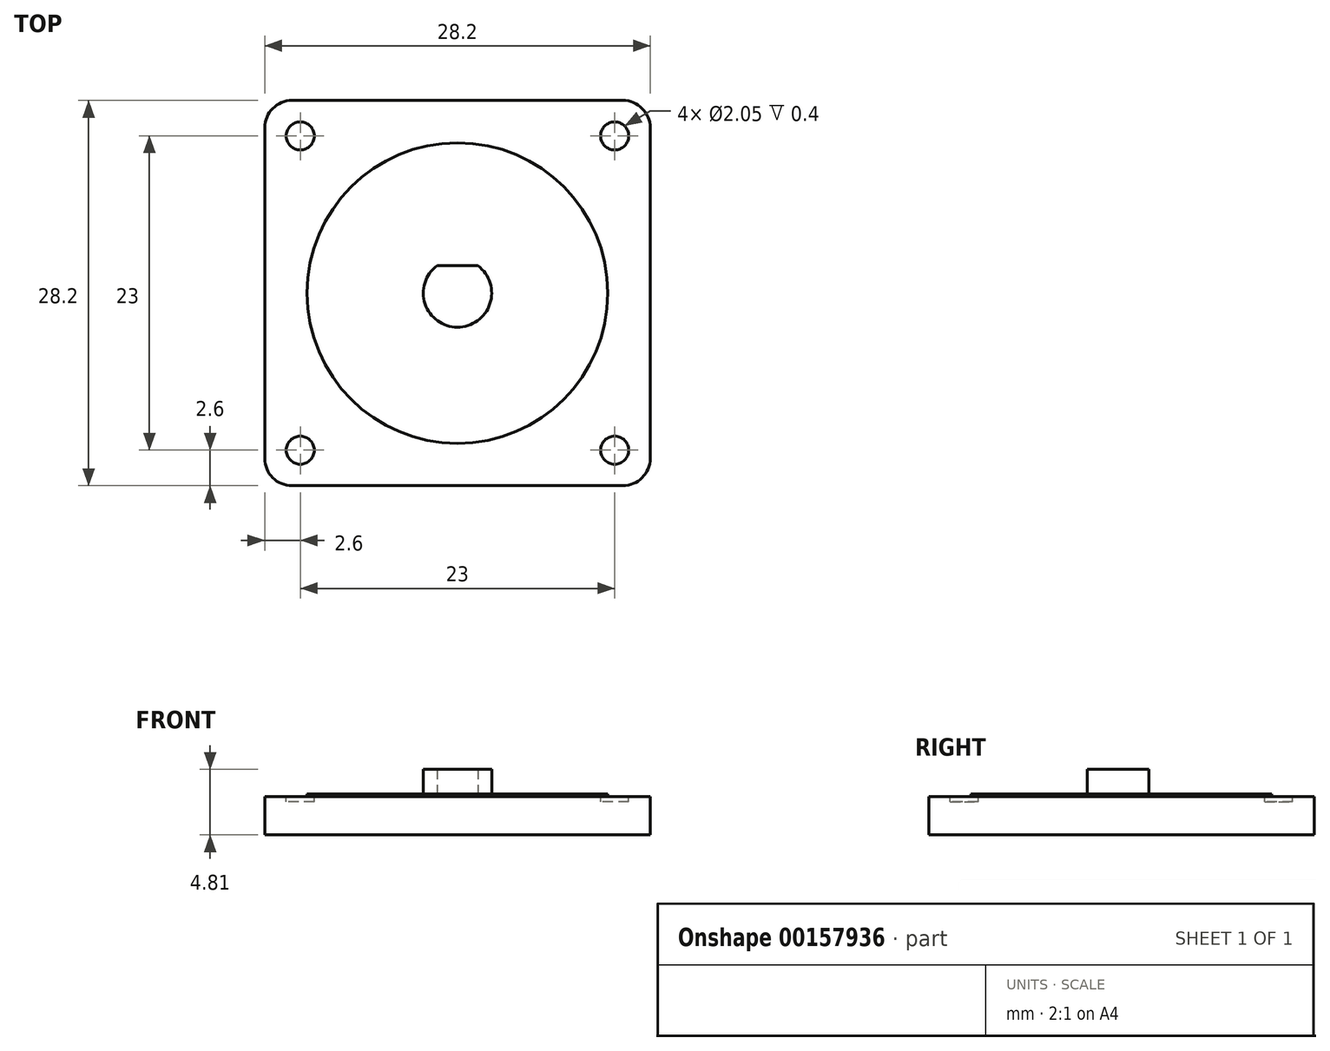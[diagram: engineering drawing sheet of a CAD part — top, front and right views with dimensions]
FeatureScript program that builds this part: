
annotation { "Feature Type Name" : "Feature", "Feature Type Description" : "" }
export const myFeature = defineFeature(function(context is Context, id is Id, definition is map)
    precondition{}
    {
        {
            assignVariable(context, id + "F0", {"name" : "h", "anyValue" : 2.81});
        }
        {
            assignVariable(context, id + "F1", {"name" : "Sd", "anyValue" : 0.4});
        }
        {
            assignVariable(context, id + "F2", {"name" : "Rh", "anyValue" : 0.2});
        }
        {
            assignVariable(context, id + "F3", {"name" : "Pl", "anyValue" : 2});
        }
        {
            var Q0;
            Q0=qCreatedBy(makeId("Top.planeOp"),FACE);
            var sketch = newSketch(context, id + "F4", { "sketchPlane" : qUnion([Q0])});
            skLineSegment(sketch, "E0.bottom", {"start": v(12.1, 14.1) * mm, "end": v(-12.1, 14.1) * mm});
            skLineSegment(sketch, "E0.top", {"start": v(12.1, -14.1) * mm, "end": v(-12.1, -14.1) * mm});
            skLineSegment(sketch, "E0.left", {"start": v(14.1, 12.1) * mm, "end": v(14.1, -12.1) * mm});
            skLineSegment(sketch, "E0.right", {"start": v(-14.1, 12.1) * mm, "end": v(-14.1, -12.1) * mm});
            skPoint(sketch, "E0.middle", {"position": v(0, 0) * mm});
            skCircle(sketch, "E1", {"center": v(0, 0) * mm, "radius": 11 * mm});
            skPoint(sketch, "E2.visualSharp", {"position": v(14.1, 14.1) * mm});
            skArc(sketch, "E2.filletArc", {"start": v(14.1, 12.1) * mm, "mid": v(13.51, 13.51) * mm, "end": v(12.1, 14.1) * mm});
            skPoint(sketch, "E3.visualSharp", {"position": v(14.1, -14.1) * mm});
            skArc(sketch, "E3.filletArc", {"start": v(12.1, -14.1) * mm, "mid": v(13.51, -13.51) * mm, "end": v(14.1, -12.1) * mm});
            skPoint(sketch, "E4.visualSharp", {"position": v(-14.1, -14.1) * mm});
            skArc(sketch, "E4.filletArc", {"start": v(-14.1, -12.1) * mm, "mid": v(-13.51, -13.51) * mm, "end": v(-12.1, -14.1) * mm});
            skPoint(sketch, "E5.visualSharp", {"position": v(-14.1, 14.1) * mm});
            skArc(sketch, "E5.filletArc", {"start": v(-12.1, 14.1) * mm, "mid": v(-13.51, 13.51) * mm, "end": v(-14.1, 12.1) * mm});
            skCircle(sketch, "E6", {"center": v(11.5, 11.5) * mm, "radius": 1.02 * mm});
            skCircle(sketch, "E7.MirrorC", {"center": v(-11.5, 11.5) * mm, "radius": 1.02 * mm});
            skCircle(sketch, "E8.MirrorC", {"center": v(11.5, -11.5) * mm, "radius": 1.02 * mm});
            skCircle(sketch, "E9.MirrorC", {"center": v(-11.5, -11.5) * mm, "radius": 1.02 * mm});
            skCircle(sketch, "E10", {"center": v(0, 0) * mm, "radius": 2.5 * mm});
            skLineSegment(sketch, "E11", {"start": v(-1.5, 2) * mm, "end": v(1.5, 2) * mm});
            skSolve(sketch);
        }
        {
            var Q0;
            Q0=makeQuery(id+"F4.imprint","IMPRINT",FACE,{"disambiguationData":[TD([[makeQuery(id+"F4.imprint","IMPRINT",EDGE,{"derivedFrom":sQuery(id+"F4.wireOp",EDGE,"E0.bottom")}),1.0]])]});
            var sketch = newSketch(context, id + "F5", { "sketchPlane" : qUnion([Q0])});
            skArc(sketch, "E12.0", {"start": v(-12.1, 14.1) * mm, "mid": v(-13.51, 13.51) * mm, "end": v(-14.1, 12.1) * mm});
            skLineSegment(sketch, "E12.1", {"start": v(12.1, 14.1) * mm, "end": v(-12.1, 14.1) * mm});
            skArc(sketch, "E12.2", {"start": v(14.1, 12.1) * mm, "mid": v(13.51, 13.51) * mm, "end": v(12.1, 14.1) * mm});
            skLineSegment(sketch, "E12.3", {"start": v(14.1, 12.1) * mm, "end": v(14.1, -12.1) * mm});
            skArc(sketch, "E12.4", {"start": v(12.1, -14.1) * mm, "mid": v(13.51, -13.51) * mm, "end": v(14.1, -12.1) * mm});
            skLineSegment(sketch, "E12.5", {"start": v(12.1, -14.1) * mm, "end": v(-12.1, -14.1) * mm});
            skArc(sketch, "E12.6", {"start": v(-14.1, -12.1) * mm, "mid": v(-13.51, -13.51) * mm, "end": v(-12.1, -14.1) * mm});
            skLineSegment(sketch, "E12.7", {"start": v(-14.1, 12.1) * mm, "end": v(-14.1, -12.1) * mm});
            skSolve(sketch);
        }
        {
            var Q0;
            Q0 = qSketchRegion(id + "F5", true);
            extrude(context, id + "F6", {"entities" : qUnion([Q0]), "depth" : (getVariable(context, 'h')) * mm});
        }
        {
            var Q0;
            Q0=makeQuery(id+"F6.opExtrude","CAP_FACE",FACE,{"disambiguationData":[OSD([sQuery(id+"F5.wireOp",EDGE,"E12.0"),sQuery(id+"F5.wireOp",EDGE,"E12.1"),sQuery(id+"F5.wireOp",EDGE,"E12.2"),sQuery(id+"F5.wireOp",EDGE,"E12.3"),sQuery(id+"F5.wireOp",EDGE,"E12.4"),sQuery(id+"F5.wireOp",EDGE,"E12.5"),sQuery(id+"F5.wireOp",EDGE,"E12.6"),sQuery(id+"F5.wireOp",EDGE,"E12.7")])],"isStart":false});
            var sketch = newSketch(context, id + "F7", { "sketchPlane" : qUnion([Q0])});
            skCircle(sketch, "E13.0", {"center": v(0, 0) * mm, "radius": 11 * mm});
            skSolve(sketch);
        }
        {
            var Q0;
            Q0=makeQuery(id+"F7.imprint","IMPRINT",FACE,{"disambiguationData":[TD([[makeQuery(id+"F7.imprint","IMPRINT",EDGE,{"derivedFrom":sQuery(id+"F7.wireOp",EDGE,"E13.0")}),-1.0]])]});
            var sketch = newSketch(context, id + "F8", { "sketchPlane" : qUnion([Q0])});
            skCircle(sketch, "E14.0", {"center": v(0, 0) * mm, "radius": 2.5 * mm});
            skLineSegment(sketch, "E14.1", {"start": v(-1.5, 2) * mm, "end": v(1.5, 2) * mm});
            skSolve(sketch);
        }
        {
            var Q0;
            Q0 = qSketchRegion(id + "F7", true);
            var Q1;
            Q1=sQuery(id+"F4.wireOp",EDGE,"E1");
            var Q2;
            Q2 = qConstructionFilter(qBodyType(qCreatedBy(id + "F7" ,EDGE), BodyType.WIRE), ConstructionObject.NO);
            extrude(context, id + "F9", {"entities" : qUnion([Q0]), "operationType" : NewBodyOperationType.ADD, "surfaceEntities" : qUnion([Q1, Q2]), "depth" : (getVariable(context, 'Rh')) * mm});
        }
        {
            var Q0;
            {var subQ0=sQuery(id+"F8.wireOp",EDGE,"E14.1");Q0=makeQuery(id+"F8.imprint","IMPRINT",FACE,{"disambiguationData":[TD([[makeQuery(id+"F8.imprint","IMPRINT",EDGE,{"derivedFrom":subQ0}),-1.0]])]});}
            extrude(context, id + "F10", {"entities" : qUnion([Q0]), "operationType" : NewBodyOperationType.ADD, "depth" : (getVariable(context, 'Pl')) * mm});
        }
        {
            var Q0;
            Q0=makeQuery(id+"F6.opExtrude","CAP_FACE",FACE,{"disambiguationData":[OSD([sQuery(id+"F5.wireOp",EDGE,"E12.0"),sQuery(id+"F5.wireOp",EDGE,"E12.1"),sQuery(id+"F5.wireOp",EDGE,"E12.2"),sQuery(id+"F5.wireOp",EDGE,"E12.3"),sQuery(id+"F5.wireOp",EDGE,"E12.4"),sQuery(id+"F5.wireOp",EDGE,"E12.5"),sQuery(id+"F5.wireOp",EDGE,"E12.6"),sQuery(id+"F5.wireOp",EDGE,"E12.7")])],"isStart":false});
            var sketch = newSketch(context, id + "F11", { "sketchPlane" : qUnion([Q0])});
            skCircle(sketch, "E15.0", {"center": v(-11.5, 11.5) * mm, "radius": 1.02 * mm});
            skCircle(sketch, "E15.1", {"center": v(11.5, 11.5) * mm, "radius": 1.02 * mm});
            skCircle(sketch, "E15.2", {"center": v(11.5, -11.5) * mm, "radius": 1.02 * mm});
            skCircle(sketch, "E15.3", {"center": v(-11.5, -11.5) * mm, "radius": 1.02 * mm});
            skSolve(sketch);
        }
        {
            var Q0;
            Q0 = qSketchRegion(id + "F11", true);
            extrude(context, id + "F12", {"entities" : qUnion([Q0]), "operationType" : NewBodyOperationType.REMOVE, "oppositeDirection" : true, "depth" : (getVariable(context, 'Sd')) * mm});
        }
    });
